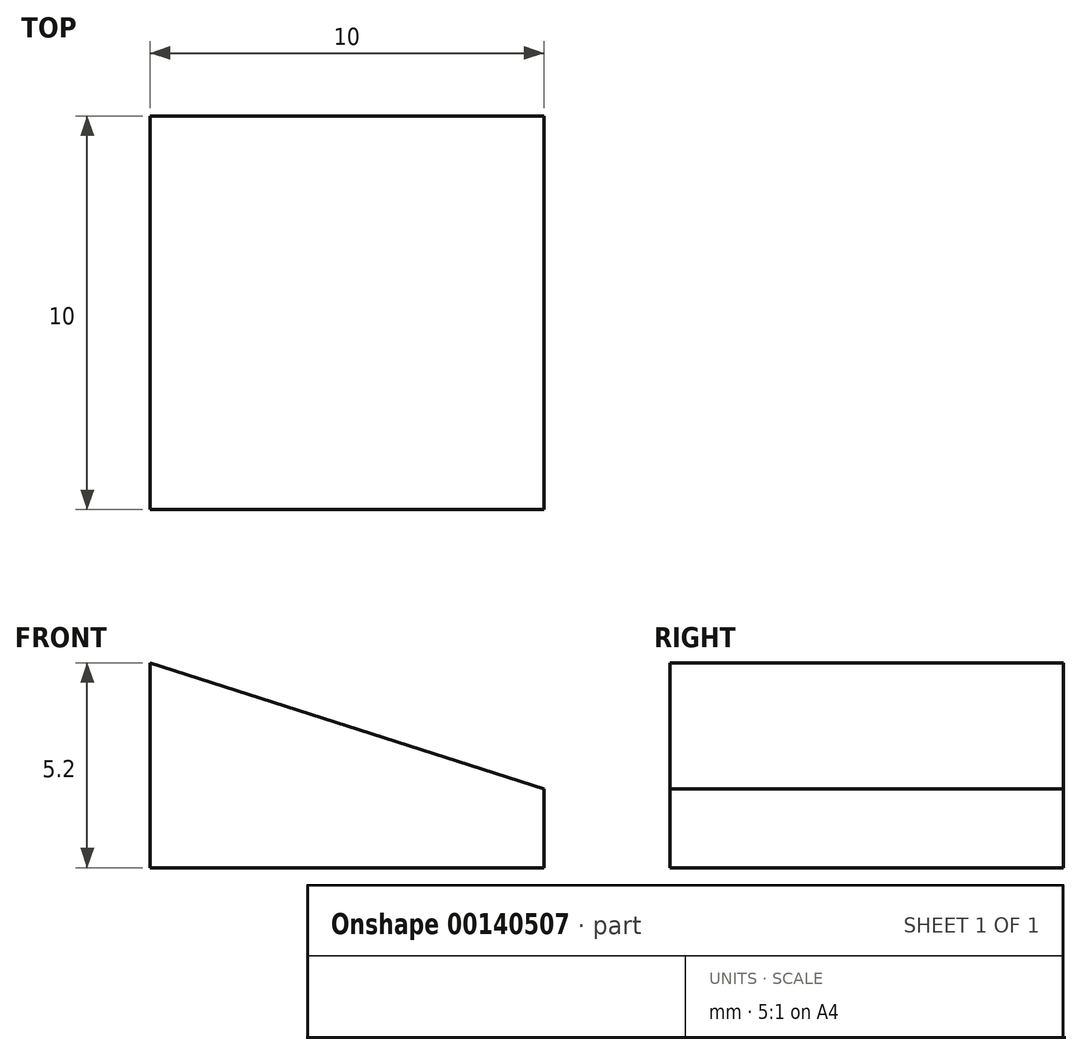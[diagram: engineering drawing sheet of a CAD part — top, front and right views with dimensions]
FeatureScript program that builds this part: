
annotation { "Feature Type Name" : "Feature", "Feature Type Description" : "" }
export const myFeature = defineFeature(function(context is Context, id is Id, definition is map)
    precondition{}
    {
        {
            var Q0;
            Q0=qCreatedBy(makeId("Front.planeOp"),FACE);
            var sketch = newSketch(context, id + "F0", { "sketchPlane" : qUnion([Q0])});
            skLineSegment(sketch, "E0", {"start": v(0, 0) * mm, "end": v(0, 2) * mm});
            skLineSegment(sketch, "E1", {"start": v(0, 2) * mm, "end": v(-10, 5.2) * mm});
            skLineSegment(sketch, "E2", {"start": v(0, 0) * mm, "end": v(-10, 0) * mm});
            skLineSegment(sketch, "E3", {"start": v(-10, 0) * mm, "end": v(-10, 5.2) * mm});
            skSolve(sketch);
        }
        {
            var Q0;
            Q0 = qSketchRegion(id + "F0", true);
            var Q1;
            Q1=makeQuery(id+"F0.imprint","IMPRINT",FACE,{"disambiguationData":[TD([[makeQuery(id+"F0.imprint","IMPRINT",EDGE,{"derivedFrom":sQuery(id+"F0.wireOp",EDGE,"E0")}),1.0]])]});
            extrude(context, id + "F1", {"entities" : qUnion([Q0, Q1]), "depth" : 10 * mm});
        }
    });
